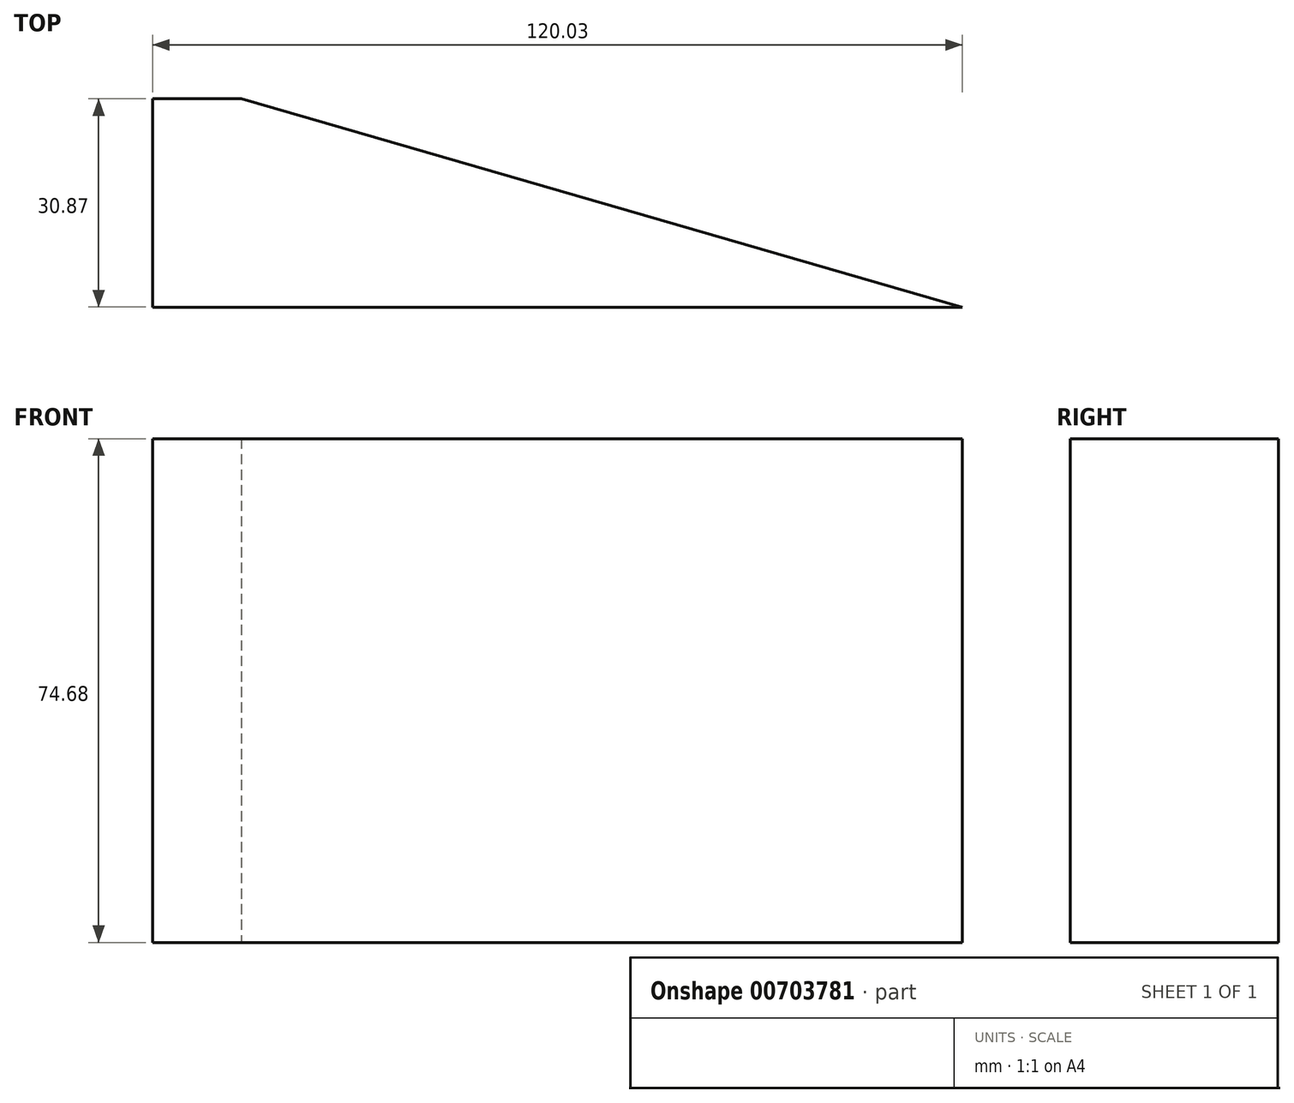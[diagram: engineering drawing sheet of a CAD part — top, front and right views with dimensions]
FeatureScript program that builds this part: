
annotation { "Feature Type Name" : "Feature", "Feature Type Description" : "" }
export const myFeature = defineFeature(function(context is Context, id is Id, definition is map)
    precondition{}
    {
        {
            var Q0;
            Q0=qCreatedBy(makeId("Top.planeOp"),FACE);
            var sketch = newSketch(context, id + "F0", { "sketchPlane" : qUnion([Q0])});
            skLineSegment(sketch, "E0", {"start": v(-62.8, 17.8) * mm, "end": v(-62.8, -30.87) * mm});
            skLineSegment(sketch, "E1", {"start": v(-62.8, -30.87) * mm, "end": v(69.4, -30.87) * mm});
            skLineSegment(sketch, "E2", {"start": v(69.4, -30.87) * mm, "end": v(-37.48, 0) * mm});
            skLineSegment(sketch, "E3", {"start": v(-37.48, 0) * mm, "end": v(-37.48, 17.8) * mm});
            skLineSegment(sketch, "E4", {"start": v(-37.48, 17.8) * mm, "end": v(-62.8, 17.8) * mm});
            skSolve(sketch);
        }
        {
            var Q0;
            Q0=makeQuery(id+"F0.imprint","IMPRINT",FACE,{"disambiguationData":[TD([[makeQuery(id+"F0.imprint","IMPRINT",EDGE,{"derivedFrom":sQuery(id+"F0.wireOp",EDGE,"E0")}),1.0]])]});
            extrude(context, id + "F1", {"entities" : qUnion([Q0]), "depth" : 74.68 * mm, "offsetDistance" : 25.4 * mm});
        }
        {
            var Q0;
            Q0=qCreatedBy(makeId("Top.planeOp"),FACE);
            var sketch = newSketch(context, id + "F2", { "sketchPlane" : qUnion([Q0])});
            skLineSegment(sketch, "E5.bottom", {"start": v(-65.05, 0) * mm, "end": v(0, 0) * mm});
            skLineSegment(sketch, "E5.top", {"start": v(-65.05, 38.8) * mm, "end": v(0, 38.8) * mm});
            skLineSegment(sketch, "E5.left", {"start": v(-65.05, 0) * mm, "end": v(-65.05, 38.8) * mm});
            skLineSegment(sketch, "E5.right", {"start": v(0, 0) * mm, "end": v(0, 38.8) * mm});
            skSolve(sketch);
        }
        {
            var Q0;
            Q0 = qSketchRegion(id + "F2", true);
            extrude(context, id + "F3", {"entities" : qUnion([Q0]), "operationType" : NewBodyOperationType.REMOVE, "depth" : 123.19 * mm, "offsetDistance" : 25.4 * mm});
        }
        {
            var Q0;
            Q0=qCreatedBy(makeId("Top.planeOp"),FACE);
            var sketch = newSketch(context, id + "F4", { "sketchPlane" : qUnion([Q0])});
            skLineSegment(sketch, "E6.bottom", {"start": v(-58.76, 0) * mm, "end": v(-134.12, 0) * mm});
            skLineSegment(sketch, "E6.top", {"start": v(-58.76, -42.81) * mm, "end": v(-134.12, -42.81) * mm});
            skLineSegment(sketch, "E6.left", {"start": v(-58.76, 0) * mm, "end": v(-58.76, -42.81) * mm});
            skLineSegment(sketch, "E6.right", {"start": v(-134.12, 0) * mm, "end": v(-134.12, -42.81) * mm});
            skSolve(sketch);
        }
        {
            var Q0;
            Q0 = qSketchRegion(id + "F4", true);
            extrude(context, id + "F5", {"entities" : qUnion([Q0]), "operationType" : NewBodyOperationType.REMOVE, "depth" : 78.74 * mm, "offsetDistance" : 25.4 * mm});
        }
        {
            var Q0;
            Q0=qCreatedBy(makeId("Top.planeOp"),FACE);
            var sketch = newSketch(context, id + "F6", { "sketchPlane" : qUnion([Q0])});
            skLineSegment(sketch, "E7.bottom", {"start": v(-50.63, 0) * mm, "end": v(-66, 0) * mm});
            skLineSegment(sketch, "E7.top", {"start": v(-50.63, -37.42) * mm, "end": v(-66, -37.42) * mm});
            skLineSegment(sketch, "E7.left", {"start": v(-50.63, 0) * mm, "end": v(-50.63, -37.42) * mm});
            skLineSegment(sketch, "E7.right", {"start": v(-66, 0) * mm, "end": v(-66, -37.42) * mm});
            skSolve(sketch);
        }
        {
            var Q0;
            Q0 = qSketchRegion(id + "F6", true);
            extrude(context, id + "F7", {"entities" : qUnion([Q0]), "operationType" : NewBodyOperationType.REMOVE, "depth" : 116.84 * mm, "offsetDistance" : 25.4 * mm});
        }
    });
